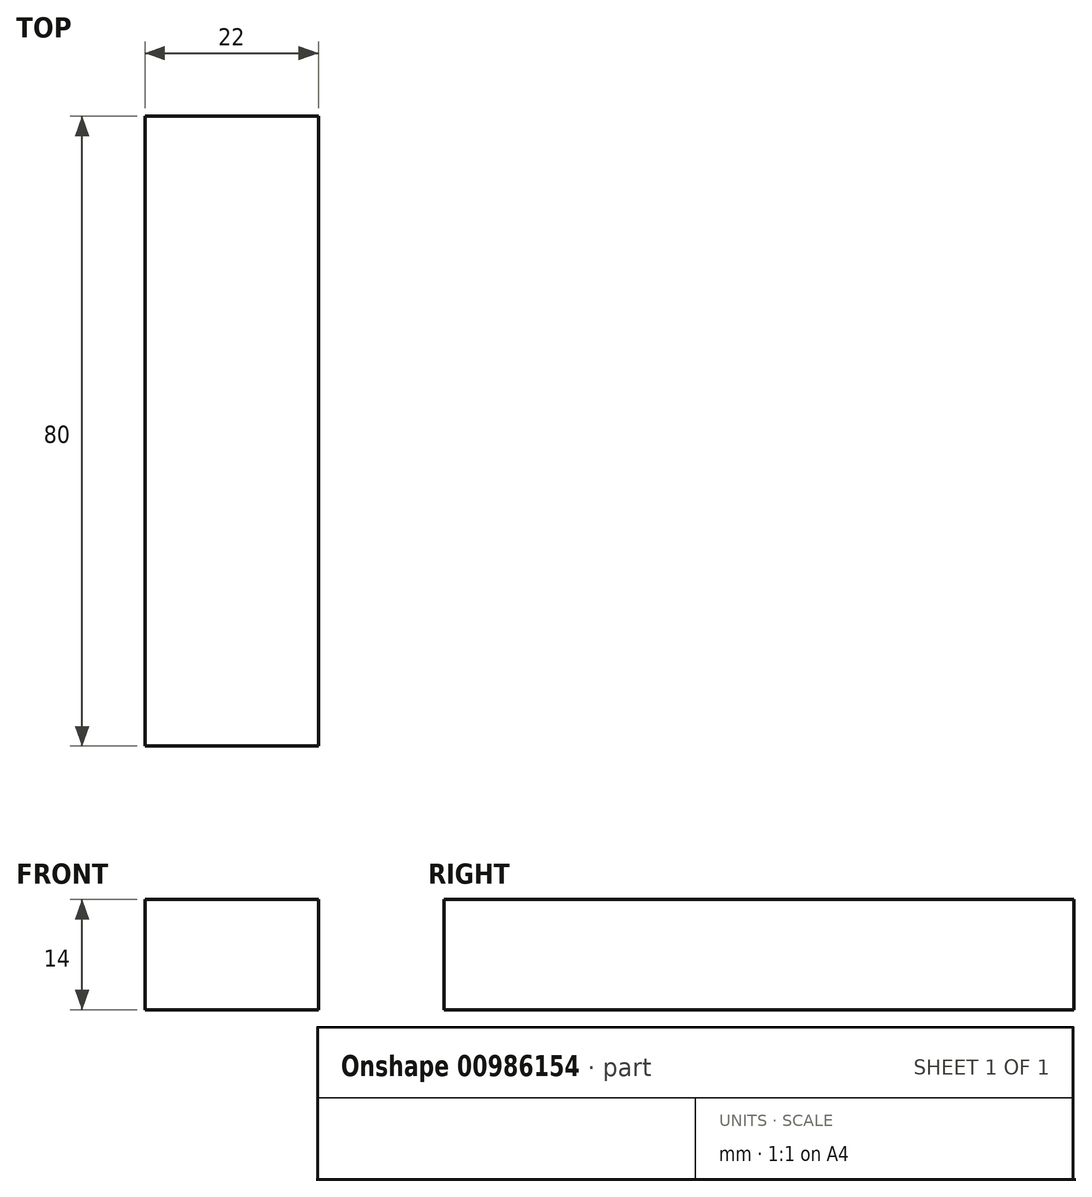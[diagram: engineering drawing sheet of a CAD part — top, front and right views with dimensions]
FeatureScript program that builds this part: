
annotation { "Feature Type Name" : "Feature", "Feature Type Description" : "" }
export const myFeature = defineFeature(function(context is Context, id is Id, definition is map)
    precondition{}
    {
        {
            var Q0;
            Q0=qCreatedBy(makeId("Front.planeOp"),FACE);
            var sketch = newSketch(context, id + "F0", { "sketchPlane" : qUnion([Q0])});
            skLineSegment(sketch, "E0.bottom", {"start": v(-11, 7) * mm, "end": v(11, 7) * mm});
            skLineSegment(sketch, "E0.top", {"start": v(-11, -7) * mm, "end": v(11, -7) * mm});
            skLineSegment(sketch, "E0.left", {"start": v(-11, 7) * mm, "end": v(-11, -7) * mm});
            skLineSegment(sketch, "E0.right", {"start": v(11, 7) * mm, "end": v(11, -7) * mm});
            skLineSegment(sketch, "E1", {"start": v(-11, 7) * mm, "end": v(11, -7) * mm, "construction": true});
            skSolve(sketch);
        }
        {
            var Q0;
            Q0 = qSketchRegion(id + "F0", true);
            extrude(context, id + "F1", {"entities" : qUnion([Q0]), "depth" : 80 * mm, "offsetDistance" : 25 * mm});
        }
    });
